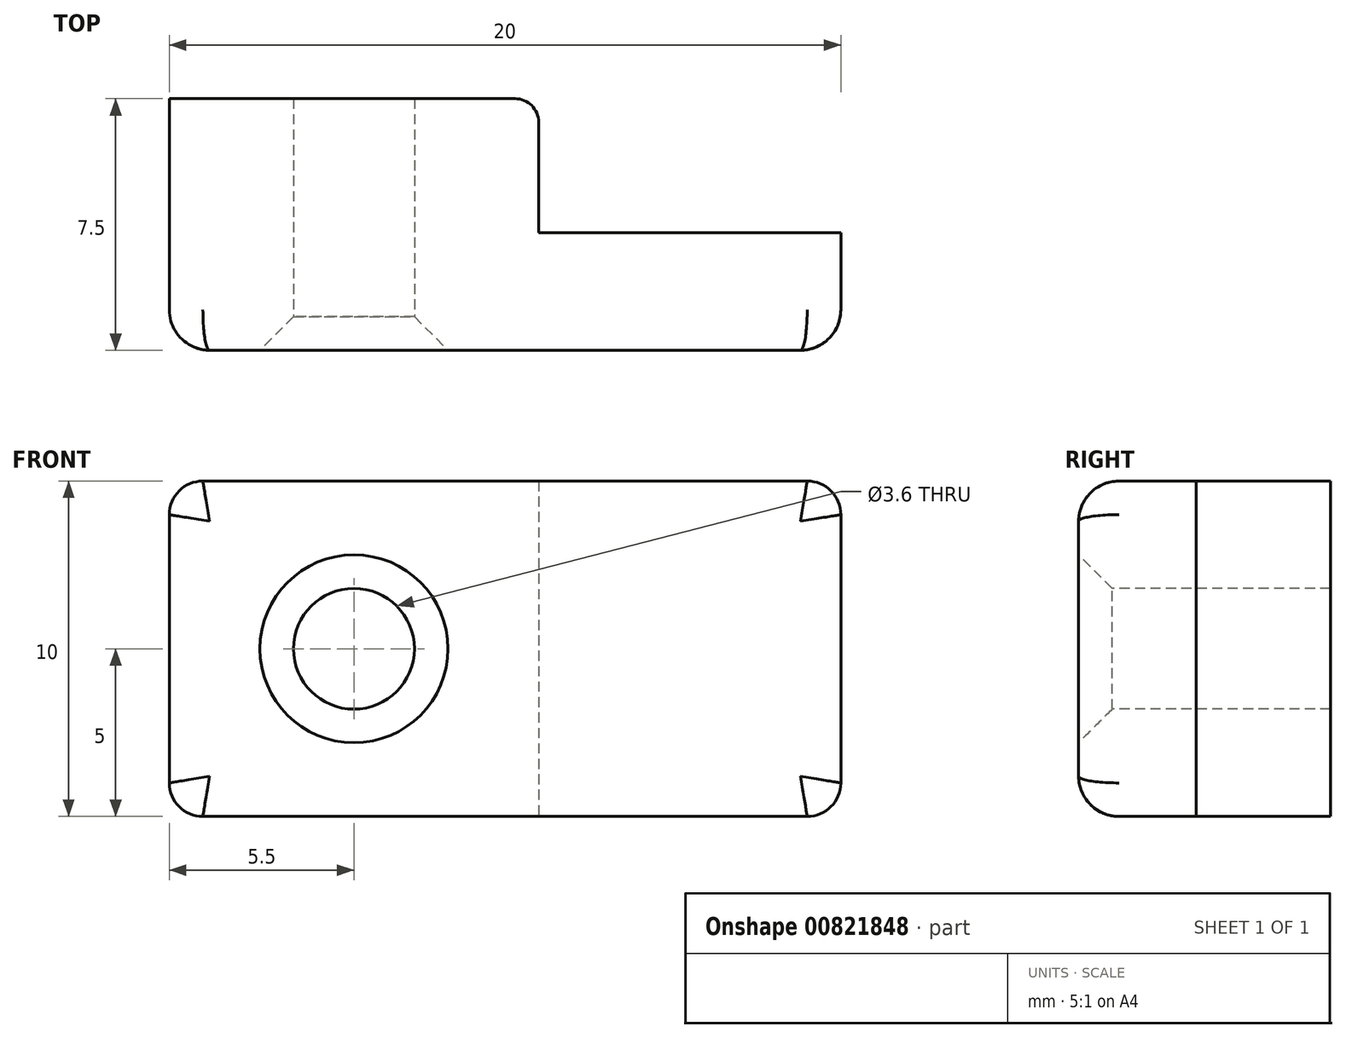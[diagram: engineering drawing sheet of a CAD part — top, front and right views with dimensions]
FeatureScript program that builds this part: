
annotation { "Feature Type Name" : "Feature", "Feature Type Description" : "" }
export const myFeature = defineFeature(function(context is Context, id is Id, definition is map)
    precondition{}
    {
        {
            var Q0;
            Q0=qCreatedBy(makeId("Top.planeOp"),FACE);
            var sketch = newSketch(context, id + "F0", { "sketchPlane" : qUnion([Q0])});
            skLineSegment(sketch, "E0", {"start": v(0, 0) * mm, "end": v(0, 4) * mm});
            skLineSegment(sketch, "E1", {"start": v(0, 4) * mm, "end": v(-7, 4) * mm});
            skLineSegment(sketch, "E2", {"start": v(-7, 4) * mm, "end": v(-7, 7.5) * mm});
            skLineSegment(sketch, "E3", {"start": v(-7, 7.5) * mm, "end": v(4, 7.5) * mm});
            skLineSegment(sketch, "E4", {"start": v(4, 7.5) * mm, "end": v(4, 3.5) * mm});
            skLineSegment(sketch, "E5", {"start": v(4, 3.5) * mm, "end": v(13, 3.5) * mm});
            skLineSegment(sketch, "E6", {"start": v(13, 3.5) * mm, "end": v(13, 0) * mm});
            skLineSegment(sketch, "E7", {"start": v(13, 0) * mm, "end": v(0, 0) * mm});
            skLineSegment(sketch, "E8", {"start": v(0, 0) * mm, "end": v(-7, 0) * mm});
            skLineSegment(sketch, "E9", {"start": v(-7, 0) * mm, "end": v(-7, 4) * mm});
            skSolve(sketch);
        }
        {
            var Q0;
            Q0 = qSketchRegion(id + "F0", true);
            extrude(context, id + "F1", {"entities" : qUnion([Q0]), "endBound" : BoundingType.SYMMETRIC, "depth" : 10 * mm, "offsetDistance" : 25 * mm});
        }
        {
            var Q0;
            Q0=makeQuery(id+"F1.opExtrude","SWEPT_FACE",FACE,{"disambiguationData":[OSD([sQuery(id+"F0.wireOp",EDGE,"E5")])]});
            var sketch = newSketch(context, id + "F2", { "sketchPlane" : qUnion([Q0])});
            skLineSegment(sketch, "E10", {"start": v(14.6, 0) * mm, "end": v(-13.36, 0) * mm, "construction": true});
            skPoint(sketch, "E10.endSnap0", {"position": v(-4, 0) * mm});
            skCircle(sketch, "E11", {"center": v(1.5, 0) * mm, "radius": 1.8 * mm});
            skCircle(sketch, "E12", {"center": v(1.5, 0) * mm, "radius": 3.5 * mm});
            skLineSegment(sketch, "E13", {"start": v(0, 8.7) * mm, "end": v(0, -8.9) * mm, "construction": true});
            skLineSegment(sketch, "E14", {"start": v(0, 7.5) * mm, "end": v(3.63, 2.78) * mm});
            skLineSegment(sketch, "E15", {"start": v(0, -7.5) * mm, "end": v(4.1, -2.34) * mm});
            skLineSegment(sketch, "E16", {"start": v(0, 7.5) * mm, "end": v(0, -7.5) * mm});
            skLineSegment(sketch, "E17", {"start": v(7.06, -7.5) * mm, "end": v(7.06, 7.65) * mm});
            skLineSegment(sketch, "E18", {"start": v(7.06, 7.65) * mm, "end": v(0, 7.5) * mm});
            skLineSegment(sketch, "E19", {"start": v(7.06, -7.5) * mm, "end": v(0, -7.5) * mm});
            skSolve(sketch);
        }
        {
            var Q0;
            Q0=makeQuery(id+"F2.imprint","IMPRINT",FACE,{"disambiguationData":[TD([[makeQuery(id+"F2.imprint","IMPRINT",EDGE,{"derivedFrom":sQuery(id+"F2.wireOp",EDGE,"E11")}),1.0]])]});
            extrude(context, id + "F3", {"entities" : qUnion([Q0]), "operationType" : NewBodyOperationType.REMOVE, "endBound" : BoundingType.SYMMETRIC, "depth" : 25 * mm, "offsetDistance" : 25 * mm});
        }
        {
            var Q0;
            Q0=makeQuery(id+"F1.opExtrude","CAP_EDGE",EDGE,{"disambiguationData":[OSD([sQuery(id+"F0.wireOp",EDGE,"E6")])],"isStart":false});
            var Q1;
            Q1=makeQuery(id+"F1.opExtrude","CAP_EDGE",EDGE,{"disambiguationData":[OSD([sQuery(id+"F0.wireOp",EDGE,"E6")])],"isStart":true});
            var Q2;
            Q2=makeQuery(id+"F1.opExtrude","CAP_EDGE",EDGE,{"disambiguationData":[OSD([sQuery(id+"F0.wireOp",EDGE,"E2")])],"isStart":false});
            var Q3;
            Q3=makeQuery(id+"F1.opExtrude","CAP_EDGE",EDGE,{"disambiguationData":[OSD([sQuery(id+"F0.wireOp",EDGE,"E2")])],"isStart":true});
            fillet(context, id + "F4", {"entities" : qUnion([Q0, Q1, Q2, Q3]), "radius" : 1 * mm, "tangentPropagation" : true, "allowEdgeOverflow" : false});
        }
        {
            var Q0;
            Q0=makeQuery(id+"F1.opExtrude","SWEPT_EDGE",EDGE,{"disambiguationData":[OSD([sQuery(id+"F0.wireOp",EDGE,"E0"),sQuery(id+"F0.wireOp",EDGE,"E7")])]});
            var Q1;
            Q1=makeQuery(id+"F1.opExtrude","SWEPT_EDGE",EDGE,{"disambiguationData":[OSD([sQuery(id+"F0.wireOp",EDGE,"E0"),sQuery(id+"F0.wireOp",EDGE,"E1")])]});
            fillet(context, id + "F5", {"entities" : qUnion([Q0, Q1]), "radius" : 1.2 * mm, "tangentPropagation" : true, "allowEdgeOverflow" : false});
        }
        {
            var Q0;
            Q0=makeQuery(id+"F1.opExtrude","SWEPT_EDGE",EDGE,{"disambiguationData":[OSD([sQuery(id+"F0.wireOp",EDGE,"E3"),sQuery(id+"F0.wireOp",EDGE,"E4")])]});
            fillet(context, id + "F6", {"entities" : qUnion([Q0]), "radius" : 0.7 * mm, "tangentPropagation" : true, "allowEdgeOverflow" : false});
        }
        {
            var Q0;
            Q0=makeQuery(id+"F3.boolean.opBoolean","INTERSECT",EDGE,{"derivedFrom":[makeQuery(id+"F1.opExtrude","SWEPT_FACE",FACE,{"disambiguationData":[OSD([sQuery(id+"F0.wireOp",EDGE,"E7"),sQuery(id+"F0.wireOp",EDGE,"E8")])]}),makeQuery(id+"F3.opExtrude","SWEPT_FACE",FACE,{"disambiguationData":[OSD([sQuery(id+"F2.wireOp",EDGE,"E11")])]})]});
            chamfer(context, id + "F7", {"entities" : qUnion([Q0]), "width" : 1 * mm, "tangentPropagation" : true});
        }
    });
